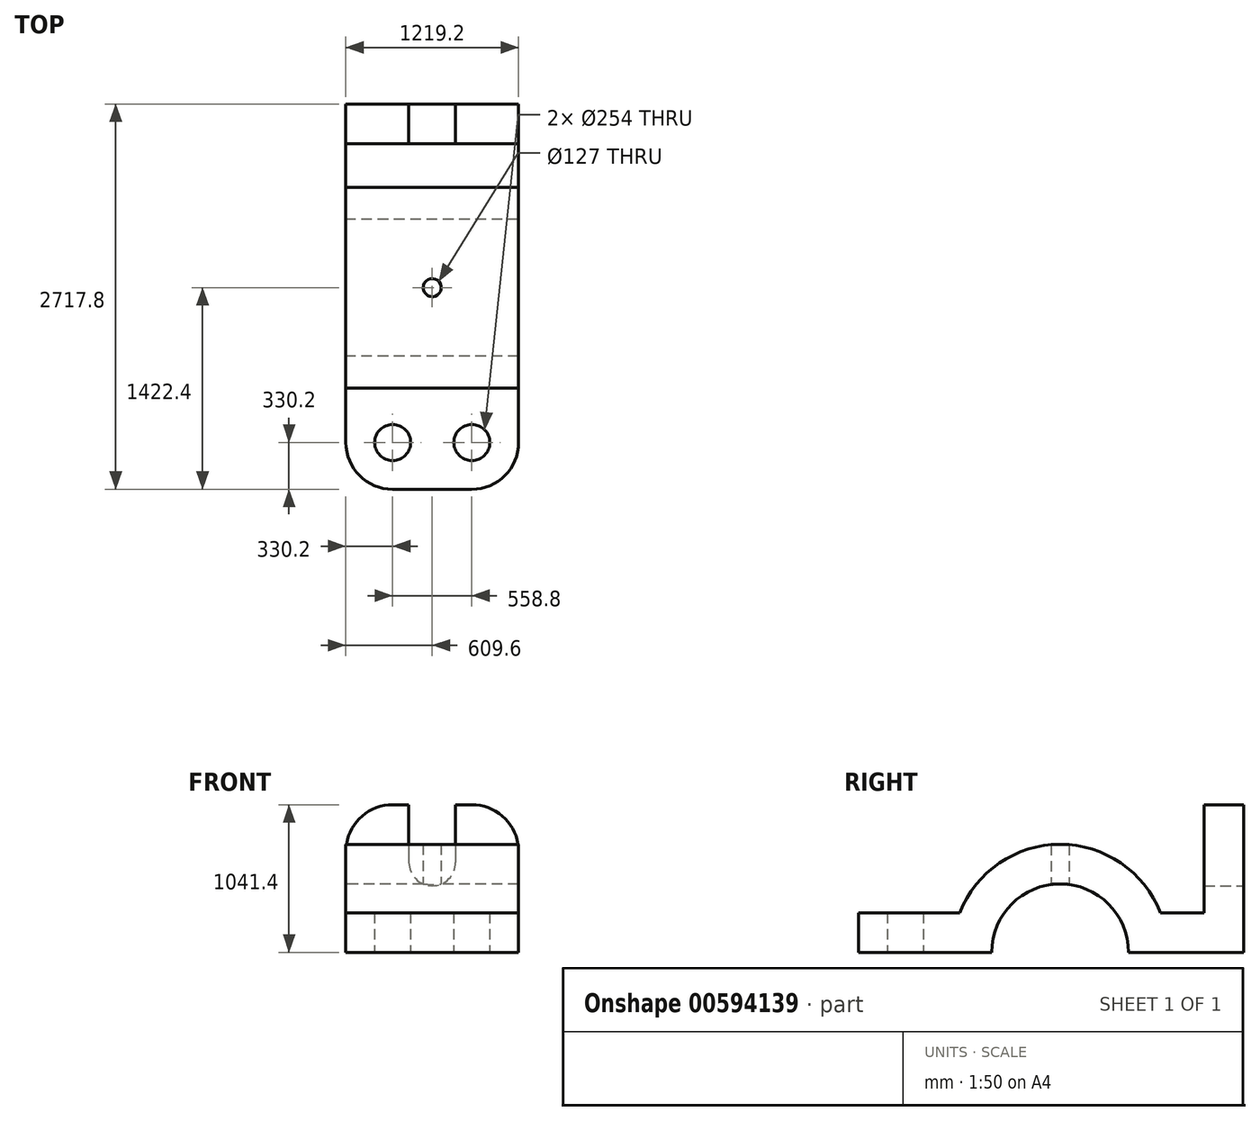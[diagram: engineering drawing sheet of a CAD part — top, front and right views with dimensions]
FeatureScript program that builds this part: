
annotation { "Feature Type Name" : "Feature", "Feature Type Description" : "" }
export const myFeature = defineFeature(function(context is Context, id is Id, definition is map)
    precondition{}
    {
        {
            var Q0;
            Q0=qCreatedBy(makeId("Right.planeOp"),FACE);
            var sketch = newSketch(context, id + "F0", { "sketchPlane" : qUnion([Q0])});
            skArc(sketch, "E0", {"start": v(482.6, 0) * mm, "mid": v(0, 482.6) * mm, "end": v(-482.6, 0) * mm});
            skArc(sketch, "E1", {"start": v(762, 0) * mm, "mid": v(0, 762) * mm, "end": v(-762, 0) * mm});
            skLineSegment(sketch, "E2.bottom", {"start": v(-1422.4, 0) * mm, "end": v(-482.6, 0) * mm});
            skLineSegment(sketch, "E2.top", {"start": v(-1422.4, 279.4) * mm, "end": v(-393.5, 279.4) * mm});
            skLineSegment(sketch, "E2.left", {"start": v(-1422.4, 0) * mm, "end": v(-1422.4, 279.4) * mm});
            skLineSegment(sketch, "E2.right", {"start": v(1295.4, 0) * mm, "end": v(1295.4, 279.4) * mm});
            skLineSegment(sketch, "E3", {"start": v(482.6, 0) * mm, "end": v(1295.4, 0) * mm});
            skLineSegment(sketch, "E4.bottom", {"start": v(1295.4, 0) * mm, "end": v(1016, 0) * mm});
            skLineSegment(sketch, "E4.top", {"start": v(1295.4, 1041.4) * mm, "end": v(1016, 1041.4) * mm});
            skLineSegment(sketch, "E4.left", {"start": v(1295.4, 0) * mm, "end": v(1295.4, 1041.4) * mm});
            skLineSegment(sketch, "E4.right", {"start": v(1016, 0) * mm, "end": v(1016, 1041.4) * mm});
            skLineSegment(sketch, "E5.trimOffspring", {"start": v(393.5, 279.4) * mm, "end": v(1295.4, 279.4) * mm});
            skSolve(sketch);
        }
        {
            var Q0;
            Q0 = qSketchRegion(id + "F0", true);
            extrude(context, id + "F1", {"entities" : qUnion([Q0]), "endBound" : BoundingType.SYMMETRIC, "depth" : 1219.2 * mm, "offsetDistance" : 25.4 * mm});
        }
        {
            var Q0;
            Q0=makeQuery(id+"F1.opExtrude","SWEPT_FACE",FACE,{"disambiguationData":[OSD([sQuery(id+"F0.wireOp",EDGE,"E4.left")])]});
            var sketch = newSketch(context, id + "F2", { "sketchPlane" : qUnion([Q0])});
            skLineSegment(sketch, "E6", {"start": v(0, 1041.4) * mm, "end": v(-165.1, 1041.4) * mm});
            skLineSegment(sketch, "E7", {"start": v(0, 1041.4) * mm, "end": v(165.1, 1041.4) * mm});
            skLineSegment(sketch, "E8", {"start": v(-165.1, 1041.4) * mm, "end": v(165.1, 1041.4) * mm});
            skLineSegment(sketch, "E9.left", {"start": v(-165.1, 1041.4) * mm, "end": v(-165.1, 635) * mm});
            skLineSegment(sketch, "E9.right", {"start": v(165.1, 1041.4) * mm, "end": v(165.1, 635) * mm});
            skArc(sketch, "E10", {"start": v(-165.1, 635) * mm, "mid": v(0, 469.9) * mm, "end": v(165.1, 635) * mm});
            skLineSegment(sketch, "E11.bottom", {"start": v(-279.4, 1041.4) * mm, "end": v(279.4, 1041.4) * mm});
            skLineSegment(sketch, "E11.top", {"start": v(-609.6, 0) * mm, "end": v(609.6, 0) * mm});
            skLineSegment(sketch, "E11.left", {"start": v(-609.6, 711.2) * mm, "end": v(-609.6, 0) * mm});
            skLineSegment(sketch, "E11.right", {"start": v(609.6, 711.2) * mm, "end": v(609.6, 0) * mm});
            skPoint(sketch, "E12.visualSharp", {"position": v(-609.6, 1041.4) * mm});
            skArc(sketch, "E12.filletArc", {"start": v(-279.4, 1041.4) * mm, "mid": v(-512.89, 944.69) * mm, "end": v(-609.6, 711.2) * mm});
            skPoint(sketch, "E13.visualSharp", {"position": v(609.6, 1041.4) * mm});
            skArc(sketch, "E13.filletArc", {"start": v(609.6, 711.2) * mm, "mid": v(512.89, 944.69) * mm, "end": v(279.4, 1041.4) * mm});
            skSolve(sketch);
        }
        {
            var Q0;
            Q0=makeQuery(id+"F1.opExtrude","SWEPT_FACE",FACE,{"disambiguationData":[OSD([sQuery(id+"F0.wireOp",EDGE,"E2.bottom")])]});
            var sketch = newSketch(context, id + "F3", { "sketchPlane" : qUnion([Q0])});
            skLineSegment(sketch, "E14", {"start": v(0, 1422.4) * mm, "end": v(-279.4, 1422.4) * mm});
            skLineSegment(sketch, "E15", {"start": v(0, 1422.4) * mm, "end": v(279.4, 1422.4) * mm});
            skLineSegment(sketch, "E16", {"start": v(-279.4, 1422.4) * mm, "end": v(279.4, 1422.4) * mm});
            skLineSegment(sketch, "E17.bottom", {"start": v(279.4, 1422.4) * mm, "end": v(-279.4, 1422.4) * mm});
            skLineSegment(sketch, "E17.top", {"start": v(152.4, 1092.2) * mm, "end": v(-152.4, 1092.2) * mm});
            skLineSegment(sketch, "E17.left", {"start": v(279.4, 1422.4) * mm, "end": v(279.4, 1219.2) * mm});
            skLineSegment(sketch, "E17.right", {"start": v(-279.4, 1422.4) * mm, "end": v(-279.4, 1219.2) * mm});
            skCircle(sketch, "E18", {"center": v(279.4, 1092.2) * mm, "radius": 127 * mm});
            skCircle(sketch, "E19", {"center": v(-279.4, 1092.2) * mm, "radius": 127 * mm});
            skLineSegment(sketch, "E20", {"start": v(0, 482.6) * mm, "end": v(0, 0) * mm});
            skCircle(sketch, "E21", {"center": v(0, 0) * mm, "radius": 63.5 * mm});
            skLineSegment(sketch, "E22.top", {"start": v(-609.6, 482.6) * mm, "end": v(609.6, 482.6) * mm});
            skLineSegment(sketch, "E22.left", {"start": v(-609.6, 1092.2) * mm, "end": v(-609.6, 482.6) * mm});
            skLineSegment(sketch, "E22.right", {"start": v(609.6, 1092.2) * mm, "end": v(609.6, 482.6) * mm});
            skPoint(sketch, "E23.visualSharp", {"position": v(-609.6, 1422.4) * mm});
            skArc(sketch, "E23.filletArc", {"start": v(-279.4, 1422.4) * mm, "mid": v(-512.89, 1325.69) * mm, "end": v(-609.6, 1092.2) * mm});
            skPoint(sketch, "E24.visualSharp", {"position": v(609.6, 1422.4) * mm});
            skArc(sketch, "E24.filletArc", {"start": v(609.6, 1092.2) * mm, "mid": v(512.89, 1325.69) * mm, "end": v(279.4, 1422.4) * mm});
            skSolve(sketch);
        }
        {
            var Q0;
            Q0=makeQuery(id+"F3.imprint","IMPRINT",FACE,{"disambiguationData":[TD([[makeQuery(id+"F3.imprint","IMPRINT",EDGE,{"derivedFrom":sQuery(id+"F3.wireOp",EDGE,"E21")}),1.0]])]});
            extrude(context, id + "F4", {"entities" : qUnion([Q0]), "operationType" : NewBodyOperationType.REMOVE, "oppositeDirection" : true, "depth" : 990.6 * mm, "offsetDistance" : 25.4 * mm});
        }
        {
            var Q0;
            {var subQ0=sQuery(id+"F2.wireOp",EDGE,"E13.filletArc");Q0=makeQuery(id+"F2.imprint","IMPRINT",FACE,{"disambiguationData":[TD([[makeQuery(id+"F2.imprint","IMPRINT",EDGE,{"derivedFrom":subQ0}),-1.0]])]});}
            var Q1;
            {var subQ0=sQuery(id+"F2.wireOp",EDGE,"E9.left");Q1=makeQuery(id+"F2.imprint","IMPRINT",FACE,{"disambiguationData":[TD([[makeQuery(id+"F2.imprint","IMPRINT",EDGE,{"derivedFrom":subQ0}),1.0]])]});}
            var Q2;
            {var subQ0=sQuery(id+"F2.wireOp",EDGE,"E12.filletArc");Q2=makeQuery(id+"F2.imprint","IMPRINT",FACE,{"disambiguationData":[TD([[makeQuery(id+"F2.imprint","IMPRINT",EDGE,{"derivedFrom":subQ0}),-1.0]])]});}
            extrude(context, id + "F5", {"entities" : qUnion([Q0, Q1, Q2]), "operationType" : NewBodyOperationType.REMOVE, "oppositeDirection" : true, "depth" : 279.4 * mm, "offsetDistance" : 25.4 * mm});
        }
        {
            var Q0;
            {var subQ0=sQuery(id+"F3.wireOp",EDGE,"E19");var subQ1=makeQuery(id+"F3.imprint","INTERSECT",VERTEX,{"derivedFrom":[sQuery(id+"F3.wireOp",EDGE,"E17.top"),subQ0]});Q0=makeQuery(id+"F3.imprint","IMPRINT",FACE,{"disambiguationData":[TD([[makeQuery(id+"F3.imprint","IMPRINT",EDGE,{"disambiguationData":[TD([[subQ1,-1.0]])],"derivedFrom":subQ0}),1.0]])]});}
            var Q1;
            {var subQ0=sQuery(id+"F3.wireOp",EDGE,"E18");var subQ1=makeQuery(id+"F3.imprint","INTERSECT",VERTEX,{"derivedFrom":[sQuery(id+"F3.wireOp",EDGE,"E17.top"),subQ0]});Q1=makeQuery(id+"F3.imprint","IMPRINT",FACE,{"disambiguationData":[TD([[makeQuery(id+"F3.imprint","IMPRINT",EDGE,{"disambiguationData":[TD([[subQ1,1.0]])],"derivedFrom":subQ0}),1.0]])]});}
            var Q2;
            {var subQ0=sQuery(id+"F3.wireOp",EDGE,"E23.filletArc");Q2=makeQuery(id+"F3.imprint","IMPRINT",FACE,{"disambiguationData":[TD([[makeQuery(id+"F3.imprint","IMPRINT",EDGE,{"derivedFrom":subQ0}),-1.0]])]});}
            var Q3;
            {var subQ0=sQuery(id+"F3.wireOp",EDGE,"E24.filletArc");Q3=makeQuery(id+"F3.imprint","IMPRINT",FACE,{"disambiguationData":[TD([[makeQuery(id+"F3.imprint","IMPRINT",EDGE,{"derivedFrom":subQ0}),-1.0]])]});}
            extrude(context, id + "F6", {"entities" : qUnion([Q0, Q1, Q2, Q3]), "operationType" : NewBodyOperationType.REMOVE, "oppositeDirection" : true, "depth" : 279.4 * mm, "offsetDistance" : 25.4 * mm});
        }
    });
